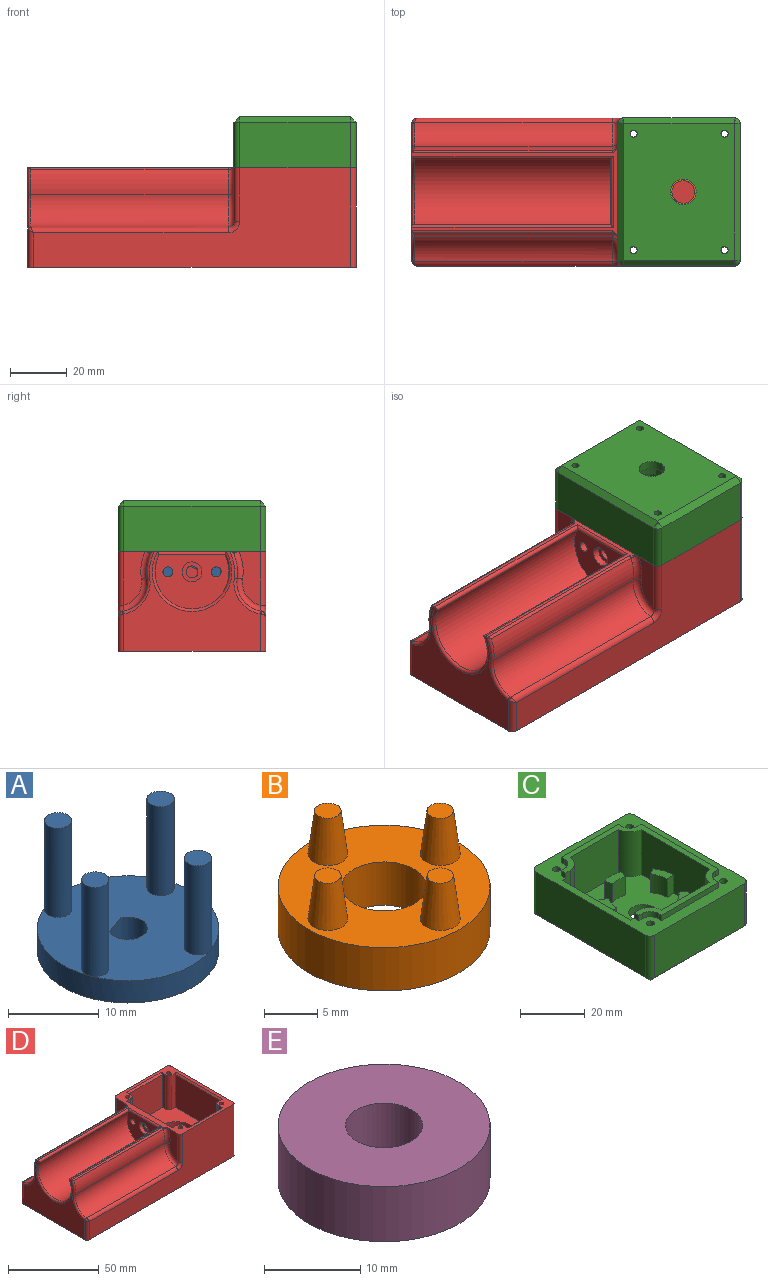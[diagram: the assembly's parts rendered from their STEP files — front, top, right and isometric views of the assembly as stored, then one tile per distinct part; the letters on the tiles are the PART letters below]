
ASSEMBLY  parts=5 mates=7
PART A: 13 faces, bbox 20x20x15 mm
  f0: cylinder r=2.15mm len=4.3mm, axis (0,0,-1), area 30.6mm2, adj f2,f3,f4
  f1: cylinder r=10mm len=20mm, axis (0,0,-1), area 188.5mm2, adj f3,f4
  f2: plane 3x2.8mm, normal (0.34,-0.94,0), area 8.9mm2, adj f0,f3,f4
  f3: plane 20x20mm, normal (0,0,1), area 272.6mm2, adj f0,f1,f2,f5,f7,f9,f11
  f4: plane 20x20mm, normal (0,0,-1), area 300.9mm2, adj f0,f1,f2
  f5: cylinder r=1.5mm len=12mm, axis (0,0,-1), area 113.1mm2, adj f3,f6
  f6: plane 3x3mm, normal (0,0,1), area 7.1mm2, adj f5
  f7: cylinder r=1.5mm len=12mm, axis (0,0,-1), area 113.1mm2, adj f3,f8
  f8: plane 3x3mm, normal (0,0,1), area 7.1mm2, adj f7
  f9: cylinder r=1.5mm len=12mm, axis (0,0,-1), area 113.1mm2, adj f3,f10
  f10: plane 3x3mm, normal (0,0,1), area 7.1mm2, adj f9
  f11: cylinder r=1.5mm len=12mm, axis (0,0,-1), area 113.1mm2, adj f3,f12
  f12: plane 3x3mm, normal (0,0,1), area 7.1mm2, adj f11
PART B: 12 faces, bbox 20x20x10 mm
  f0: cylinder r=10mm len=20mm, axis (0,0,-1), area 314.2mm2, adj f2,f3
  f1: cylinder r=4mm len=8mm, axis (0,0,-1), area 125.7mm2, adj f2,f3
  f2: plane 20x20mm, normal (0,0,1), area 219.7mm2, adj f0,f1,f5,f7,f9,f11
  f3: plane 20x20mm, normal (0,0,-1), area 263.9mm2, adj f0,f1
  f4: plane 2.5x2.5mm, normal (0,0,1), area 4.9mm2, adj f5
  f5: cone r=1.25mm half-angle=7.1deg, axis (0,0,-1), area 49.5mm2, adj f2,f4
  f6: plane 2.5x2.5mm, normal (0,0,1), area 4.9mm2, adj f7
  f7: cone r=1.25mm half-angle=7.1deg, axis (0,0,-1), area 49.5mm2, adj f2,f6
  f8: plane 2.5x2.5mm, normal (0,0,1), area 4.9mm2, adj f9
  f9: cone r=1.25mm half-angle=7.1deg, axis (0,0,-1), area 49.5mm2, adj f2,f8
  f10: plane 2.5x2.5mm, normal (0,0,1), area 4.9mm2, adj f11
  f11: cone r=1.25mm half-angle=7.1deg, axis (0,0,-1), area 49.5mm2, adj f2,f10
PART C: 77 faces, bbox 43x52x20 mm
  f0: plane 52x43mm, normal (0,0,1), area 717.4mm2, adj f1,f2,f3,f4,f5,f6,f7,f8
  f1: plane 48x16mm, normal (1,0,0), area 768mm2, adj f0,f2,f8,f76
  f2: cylinder r=2mm len=16mm, axis (0,0,1), area 50.3mm2, adj f0,f1,f3,f74
  f3: plane 39x16mm, normal (0,1,0), area 624mm2, adj f0,f2,f4,f72
  f4: cylinder r=2mm len=16mm, axis (0,0,1), area 50.3mm2, adj f0,f3,f5,f70
  f5: plane 48x16mm, normal (-1,0,0), area 768mm2, adj f0,f4,f6,f69
  f6: cylinder r=2mm len=16mm, axis (0,0,1), area 50.3mm2, adj f0,f5,f7,f71
  f7: plane 39x16mm, normal (0,-1,0), area 624mm2, adj f0,f6,f8,f73
  f8: cylinder r=2mm len=16mm, axis (0,0,1), area 50.3mm2, adj f0,f1,f7,f75
  f9: cylinder r=4.5mm len=9mm, axis (0,0,-1), area 84.8mm2, adj f14,f43
  f10: cylinder r=1.25mm len=18mm, axis (0,0,-1), area 141.4mm2, adj f0,f14
  f11: cylinder r=1.25mm len=18mm, axis (0,0,-1), area 141.4mm2, adj f0,f14
  f12: cylinder r=1.25mm len=18mm, axis (0,0,-1), area 141.4mm2, adj f0,f14
  f13: cylinder r=1.25mm len=18mm, axis (0,0,-1), area 141.4mm2, adj f0,f14
  f14: plane 48x39mm, normal (0,0,-1), area 1788.7mm2, adj f9,f10,f11,f12,f13,f69,f72,f73
  f15: plane 2x2mm, normal (-1,0,0), area 4mm2, adj f0,f21,f33,f41
  f16: plane 2x1.5mm, normal (1,0,0), area 3mm2, adj f0,f17,f30,f41
  f17: plane 25x2mm, normal (0,1,0), area 50mm2, adj f0,f16,f18,f41
  f18: plane 2x1.5mm, normal (-1,0,0), area 3mm2, adj f0,f17,f31,f41
  f19: plane 2x1.5mm, normal (0,1,0), area 3mm2, adj f0,f20,f31,f41
  f20: plane 2x2mm, normal (-1,0,0), area 4mm2, adj f0,f19,f34,f41
  f21: plane 2x1.5mm, normal (0,-1,0), area 3mm2, adj f0,f15,f28,f41
  f22: plane 2x1.5mm, normal (-1,0,0), area 3mm2, adj f0,f23,f28,f41
  f23: plane 25x2mm, normal (0,-1,0), area 50mm2, adj f0,f22,f24,f41
  f24: plane 2x1.5mm, normal (1,0,0), area 3mm2, adj f0,f23,f29,f41
  f25: plane 2x1.5mm, normal (0,-1,0), area 3mm2, adj f0,f26,f29,f41
  f26: plane 34x2mm, normal (1,0,0), area 68mm2, adj f0,f25,f27,f41
  f27: plane 2x1.5mm, normal (0,1,0), area 3mm2, adj f0,f26,f30,f41
  f28: cylinder r=3.5mm len=3.5mm, axis (0,0,-1), area 11mm2, adj f0,f21,f22,f41
  f29: cylinder r=3.5mm len=3.5mm, axis (0,0,-1), area 11mm2, adj f0,f24,f25,f41
  f30: cylinder r=3.5mm len=3.5mm, axis (0,0,-1), area 11mm2, adj f0,f16,f27,f41
  f31: cylinder r=3.5mm len=3.5mm, axis (0,0,-1), area 11mm2, adj f0,f18,f19,f41
  f32: cylinder r=5.52mm len=17mm, axis (0,0,-1), area 130.5mm2, adj f33,f40,f41,f43
  f33: plane 17x3.5mm, normal (0,1,0), area 56.5mm2, adj f0,f15,f32,f41,f42,f43
  f34: plane 17x3.5mm, normal (0,-1,0), area 56.5mm2, adj f0,f20,f35,f41,f42,f43
  f35: cylinder r=5.52mm len=17mm, axis (0,0,-1), area 130.5mm2, adj f34,f36,f41,f43
  f36: plane 21x17mm, normal (0,-1,0), area 357mm2, adj f35,f37,f41,f43
  f37: cylinder r=5.52mm len=17mm, axis (0,0,-1), area 130.5mm2, adj f36,f38,f41,f43
  f38: plane 30x17mm, normal (-1,0,0), area 510mm2, adj f37,f39,f41,f43
  f39: cylinder r=5.52mm len=17mm, axis (0,0,-1), area 130.5mm2, adj f38,f40,f41,f43
  f40: plane 21x17mm, normal (0,1,0), area 357mm2, adj f32,f39,f41,f43
  f41: plane 44x35mm, normal (0,0,1), area 225.3mm2, adj f15,f16,f17,f18,f19,f20,f21,f22
  f42: plane 30x15mm, normal (1,0,0), area 450mm2, adj f0,f33,f34,f43
  f43: plane 40x34.5mm, normal (0,0,1), area 1108.4mm2, adj f9,f32,f33,f34,f35,f36,f37,f38
  f44: plane 7x2.9mm, normal (0.97,-0.26,0), area 21mm2, adj f43,f45,f47,f48
  f45: cylinder r=14mm len=7.25mm, axis (0,0,-1), area 51.3mm2, adj f43,f44,f46,f48
  f46: plane 7x2.9mm, normal (-0.97,-0.26,0), area 21mm2, adj f43,f45,f47,f48
  f47: cylinder r=11mm len=7mm, axis (0,0,-1), area 40.3mm2, adj f43,f44,f46,f48
  f48: plane 7.25x3.38mm, normal (0,0,1), area 19.6mm2, adj f44,f45,f46,f47
  f49: plane 7x2.52mm, normal (0.54,0.84,0), area 21mm2, adj f43,f50,f52,f53
  f50: cylinder r=14mm len=7mm, axis (0,0,-1), area 51.3mm2, adj f43,f49,f51,f53
  f51: plane 7x3mm, normal (-0.05,-1,0), area 21mm2, adj f43,f50,f52,f53
  f52: cylinder r=11mm len=7mm, axis (0,0,-1), area 40.3mm2, adj f43,f49,f51,f53
  f53: plane 7.05x4.76mm, normal (0,0,1), area 19.6mm2, adj f49,f50,f51,f52
  f54: plane 7x2.33mm, normal (-0.63,0.78,0), area 21mm2, adj f43,f55,f57,f58
  f55: cylinder r=14mm len=7mm, axis (0,0,-1), area 51.3mm2, adj f43,f54,f56,f58
  f56: plane 7x2.8mm, normal (0.93,-0.36,0), area 21mm2, adj f43,f55,f57,f58
  f57: cylinder r=11mm len=7mm, axis (0,0,-1), area 40.3mm2, adj f43,f54,f56,f58
  f58: plane 6.94x6.15mm, normal (0,0,1), area 19.6mm2, adj f54,f55,f56,f57
  f59: plane 7x2.8mm, normal (-0.93,-0.36,0), area 21mm2, adj f43,f60,f62,f63
  f60: cylinder r=14mm len=7mm, axis (0,0,-1), area 51.3mm2, adj f43,f59,f61,f63
  f61: plane 7x2.33mm, normal (0.63,0.78,0), area 21mm2, adj f43,f60,f62,f63
  f62: cylinder r=11mm len=7mm, axis (0,0,-1), area 40.3mm2, adj f43,f59,f61,f63
  f63: plane 6.94x6.15mm, normal (0,0,1), area 19.6mm2, adj f59,f60,f61,f62
  f64: plane 7x3mm, normal (0.05,-1,0), area 21mm2, adj f43,f65,f67,f68
  f65: cylinder r=14mm len=7mm, axis (0,0,-1), area 51.3mm2, adj f43,f64,f66,f68
  f66: plane 7x2.52mm, normal (-0.54,0.84,0), area 21mm2, adj f43,f65,f67,f68
  f67: cylinder r=11mm len=7mm, axis (0,0,-1), area 40.3mm2, adj f43,f64,f66,f68
  f68: plane 7.05x4.76mm, normal (0,0,1), area 19.6mm2, adj f64,f65,f66,f67
  f69: plane 48x2mm, normal (-0.71,0,-0.71), area 135.8mm2, adj f5,f14,f70,f71
  f70: cone r=2mm half-angle=45deg, axis (0,0,1), area 4.4mm2, adj f4,f69,f72
  f71: cone r=2mm half-angle=45deg, axis (0,0,1), area 4.4mm2, adj f6,f69,f73
  f72: plane 39x2mm, normal (0,0.71,-0.71), area 110.3mm2, adj f3,f14,f70,f74
  f73: plane 39x2mm, normal (0,-0.71,-0.71), area 110.3mm2, adj f7,f14,f71,f75
  f74: cone r=2mm half-angle=45deg, axis (0,0,1), area 4.4mm2, adj f2,f72,f76
  f75: cone r=2mm half-angle=45deg, axis (0,0,1), area 4.4mm2, adj f8,f73,f76
  f76: plane 48x2mm, normal (0.71,0,-0.71), area 135.8mm2, adj f1,f14,f74,f75
PART D: 82 faces, bbox 115.5x52x37.4 mm
  f0: plane 46x37mm, normal (0,0,1), area 1227.2mm2, adj f1,f2,f3,f4,f26,f32,f33,f34
  f1: plane 27x22.1mm, normal (0,1,0), area 596.7mm2, adj f0,f40,f41,f74
  f2: plane 36x22.1mm, normal (-1,0,0), area 795.6mm2, adj f0,f37,f43,f76
  f3: plane 36x22.1mm, normal (1,0,0), area 725.2mm2, adj f0,f16,f21,f23,f33,f38,f75
  f4: plane 27x22.1mm, normal (0,-1,0), area 596.7mm2, adj f0,f34,f36,f77
  f5: cylinder r=16mm len=69.5mm, axis (-1,0,0), area 624.3mm2, adj f18,f44,f45,f64
  f6: cylinder r=16mm len=69.5mm, axis (-1,0,0), area 624.3mm2, adj f17,f48,f49,f55
  f7: plane 111.5x35.1mm, normal (0,1,0), area 2254.3mm2, adj f19,f25,f56,f58,f59,f62,f73
  f8: plane 111.5x35.1mm, normal (0,-1,0), area 2254.3mm2, adj f19,f25,f66,f67,f68,f71,f72
  f9: cylinder r=1.75mm len=3.5mm, axis (-1,0,0), area 27.5mm2, adj f13,f24
  f10: cylinder r=1.75mm len=3.5mm, axis (-1,0,0), area 27.5mm2, adj f13,f22
  f11: cylinder r=13mm len=69mm, axis (-1,0,0), area 3626.8mm2, adj f13,f50,f51,f52
  f12: plane 48x35.1mm, normal (-1,0,0), area 828.2mm2, adj f19,f25,f45,f46,f47,f49,f50,f51
  f13: plane 26x19.1mm, normal (-1,0,0), area 360.3mm2, adj f9,f10,f11,f14,f51,f52,f53
  f14: cylinder r=3.5mm len=7mm, axis (-1,0,0), area 55mm2, adj f13,f15
  f15: plane 7x7mm, normal (-1,0,0), area 24.6mm2, adj f14,f16
  f16: cylinder r=2.1mm len=4.2mm, axis (-1,0,0), area 39.6mm2, adj f3,f15
  f17: cylinder r=10.27mm len=69.5mm, axis (1,0,0), area 1105.7mm2, adj f6,f47,f57,f59,f61
  f18: cylinder r=10.27mm len=69.5mm, axis (1,0,0), area 1105.7mm2, adj f5,f46,f65,f68,f69
  f19: plane 115.51x52.01mm, normal (0,0,1), area 680.8mm2, adj f7,f8,f12,f20,f30,f31,f32,f33
  f20: plane 48x35.1mm, normal (1,0,0), area 1684.8mm2, adj f19,f25,f72,f73
  f21: cylinder r=3mm len=6mm, axis (1,0,0), area 56.5mm2, adj f3,f22
  f22: plane 6x6mm, normal (1,0,0), area 18.7mm2, adj f10,f21
  f23: cylinder r=3mm len=6mm, axis (1,0,0), area 56.5mm2, adj f3,f24
  f24: plane 6x6mm, normal (1,0,0), area 18.7mm2, adj f9,f23
  f25: plane 115.5x52mm, normal (0,0,-1), area 5982.9mm2, adj f7,f8,f12,f20,f62,f71,f72,f73
  f26: cylinder r=11mm len=22mm, axis (0,0,1), area 483.8mm2, adj f0,f27
  f27: plane 22x22mm, normal (0,0,1), area 247.4mm2, adj f26,f28
  f28: cylinder r=6.5mm len=13mm, axis (0,0,1), area 81.7mm2, adj f27,f29
  f29: plane 13x13mm, normal (0,0,1), area 132.7mm2, adj f28
  f30: plane 18.85x7.46mm, normal (-1,0,0), area 106.1mm2, adj f19,f55,f56,f57
  f31: plane 18.85x7.46mm, normal (-1,0,0), area 106.1mm2, adj f19,f64,f65,f66
  f32: cylinder r=2.5mm len=23.1mm, axis (0,0,1), area 90.7mm2, adj f0,f19,f33,f34
  f33: plane 23.1x3.5mm, normal (0,-1,0), area 58.2mm2, adj f0,f3,f19,f32,f75
  f34: plane 23.1x3.5mm, normal (1,0,0), area 58.2mm2, adj f0,f4,f19,f32,f77
  f35: cylinder r=2.5mm len=23.1mm, axis (0,0,1), area 90.7mm2, adj f0,f19,f36,f37
  f36: plane 23.1x3.5mm, normal (-1,0,0), area 58.2mm2, adj f0,f4,f19,f35,f77
  f37: plane 23.1x3.5mm, normal (0,-1,0), area 58.3mm2, adj f0,f2,f19,f35,f76
  f38: plane 23.1x3.5mm, normal (0,1,0), area 58.2mm2, adj f0,f3,f19,f39,f75
  f39: cylinder r=2.5mm len=23.1mm, axis (0,0,1), area 90.7mm2, adj f0,f19,f38,f40
  f40: plane 23.1x3.5mm, normal (1,0,0), area 58.2mm2, adj f0,f1,f19,f39,f74
  f41: plane 23.1x3.5mm, normal (-1,0,0), area 58.3mm2, adj f0,f1,f19,f42,f74
  f42: cylinder r=2.5mm len=23.1mm, axis (0,0,1), area 90.7mm2, adj f0,f19,f41,f43
  f43: plane 23.1x3.5mm, normal (0,1,0), area 58.3mm2, adj f0,f2,f19,f42,f76
  f44: cylinder r=1mm len=70.4mm, axis (-1,0,0), area 80.6mm2, adj f5,f19,f45,f63
  f45: torus R=15mm, axis (1,0,0), area 14.8mm2, adj f5,f12,f19,f44,f46
  f46: torus R=11.27mm, axis (1,0,0), area 25.6mm2, adj f12,f18,f45,f69
  f47: torus R=11.27mm, axis (1,0,0), area 25.6mm2, adj f12,f17,f49,f61
  f48: cylinder r=1mm len=70.4mm, axis (-1,0,0), area 80.6mm2, adj f6,f19,f49,f54
  f49: torus R=15mm, axis (1,0,0), area 14.8mm2, adj f6,f12,f19,f47,f48
  f50: torus R=14mm, axis (1,0,0), area 86.8mm2, adj f11,f12,f51,f52
  f51: cylinder r=1mm len=71mm, axis (-1,0,0), area 141.5mm2, adj f11,f12,f13,f19,f50,f53
  f52: cylinder r=1mm len=71mm, axis (-1,0,0), area 141.5mm2, adj f11,f12,f13,f19,f50,f53
  f53: cylinder r=1mm len=25.2mm, axis (0,-1,0), area 37.6mm2, adj f13,f19,f51,f52
  f54: torus R=3mm, axis (-1,0,0), area 1.4mm2, adj f19,f48,f55
  f55: torus R=18mm, axis (-1,0,0), area 29.4mm2, adj f6,f19,f30,f54,f57
  f56: cylinder r=2mm len=18.85mm, axis (0,0,1), area 59.2mm2, adj f7,f19,f30,f58
  f57: torus R=8.27mm, axis (-1,0,0), area 45.7mm2, adj f17,f30,f55,f58
  f58: bspline ~4.89x4.72mm, area 13mm2, adj f7,f56,f57,f59
  f59: cylinder r=2mm len=69.49mm, axis (1,0,0), area 194.4mm2, adj f7,f17,f58,f60
  f60: bspline ~2x2mm, area 2.7mm2, adj f59,f61,f62
  f61: bspline ~1.11x1.05mm, area 0.4mm2, adj f17,f47,f60,f62
  f62: cylinder r=2mm len=13.18mm, axis (0,0,1), area 40.2mm2, adj f7,f12,f25,f60,f61
  f63: torus R=3mm, axis (-1,0,0), area 1.4mm2, adj f19,f44,f64
  f64: torus R=18mm, axis (-1,0,0), area 29.4mm2, adj f5,f19,f31,f63,f65
  f65: torus R=8.27mm, axis (-1,0,0), area 45.7mm2, adj f18,f31,f64,f67
  f66: cylinder r=2mm len=18.85mm, axis (0,0,-1), area 59.2mm2, adj f8,f19,f31,f67
  f67: bspline ~5.04x4.74mm, area 13mm2, adj f8,f65,f66,f68
  f68: cylinder r=2mm len=69.49mm, axis (1,0,0), area 194.4mm2, adj f8,f18,f67,f70
  f69: bspline ~1.11x1.05mm, area 0.4mm2, adj f18,f46,f70,f71
  f70: bspline ~2x2mm, area 2.7mm2, adj f68,f69,f71
  f71: cylinder r=2mm len=13.18mm, axis (0,0,-1), area 40.2mm2, adj f8,f12,f25,f69,f70
  f72: cylinder r=2mm len=35.1mm, axis (0,0,-1), area 110.3mm2, adj f8,f19,f20,f25
  f73: cylinder r=2mm len=35.1mm, axis (0,0,1), area 110.3mm2, adj f7,f19,f20,f25
  f74: plane 27x1mm, normal (0,0.71,0.71), area 38.2mm2, adj f1,f19,f40,f41
  f75: plane 36x1mm, normal (0.71,0,0.71), area 50.9mm2, adj f3,f19,f33,f38
  f76: plane 36x1mm, normal (-0.71,0,0.71), area 50.9mm2, adj f2,f19,f37,f43
  f77: plane 27x1mm, normal (0,-0.71,0.71), area 38.2mm2, adj f4,f19,f34,f36
  f78: cylinder r=1.25mm len=35.1mm, axis (0,0,1), area 275.7mm2, adj f19,f25
  f79: cylinder r=1.25mm len=35.1mm, axis (0,0,1), area 275.7mm2, adj f19,f25
  f80: cylinder r=1.25mm len=35.1mm, axis (0,0,1), area 275.7mm2, adj f19,f25
  f81: cylinder r=1.25mm len=35.1mm, axis (0,0,1), area 275.7mm2, adj f19,f25
PART E: 4 faces, bbox 22x22x7 mm
  f0: cylinder r=4mm len=8mm, axis (0,0,-1), area 175.9mm2, adj f2,f3
  f1: cylinder r=11mm len=22mm, axis (0,0,-1), area 483.8mm2, adj f2,f3
  f2: plane 22x22mm, normal (0,0,1), area 329.9mm2, adj f0,f1
  f3: plane 22x22mm, normal (0,0,-1), area 329.9mm2, adj f0,f1
PLACE A rot(axis=(0.61,0.51,0.61),125.6deg) t=(37.2,8.69,7.82)mm
PLACE B rot(axis=(0,0,-1),99.4deg) t=(57.2,8.69,-8.18)mm
PLACE C rot(axis=(1,0,0),180deg) t=(54.84,8.69,19.92)mm
PLACE D t=(-3.3,8.69,-8.18)mm fixed
PLACE E rot(axis=(0,0,1),90deg) t=(57.2,8.69,-15.18)mm
MATE cylindrical B.f0 <-> C.f9  axis (0,0,1) through (57.2,8.69,-3.18)mm
MATE planar D.f26 <-> E.f0  axis (0,0,1) through (57.2,8.69,-15.18)mm
MATE cylindrical D.f39 <-> C.f13  axis (0,0,1) through (39.7,-11.81,14.92)mm
MATE revolute D.f5 <-> A.f0  axis (1,0,0) through (37.2,8.69,7.82)mm
MATE planar C.f8 <-> D.f73  axis (0,0,-1) through (75.2,32.69,14.92)mm
MATE revolute B.f0 <-> E.f0  axis (0,0,-1) through (57.2,8.69,-8.18)mm
MATE slider D.f26 <-> E.f0  axis (0,0,1) through (57.2,8.69,-11.68)mm
